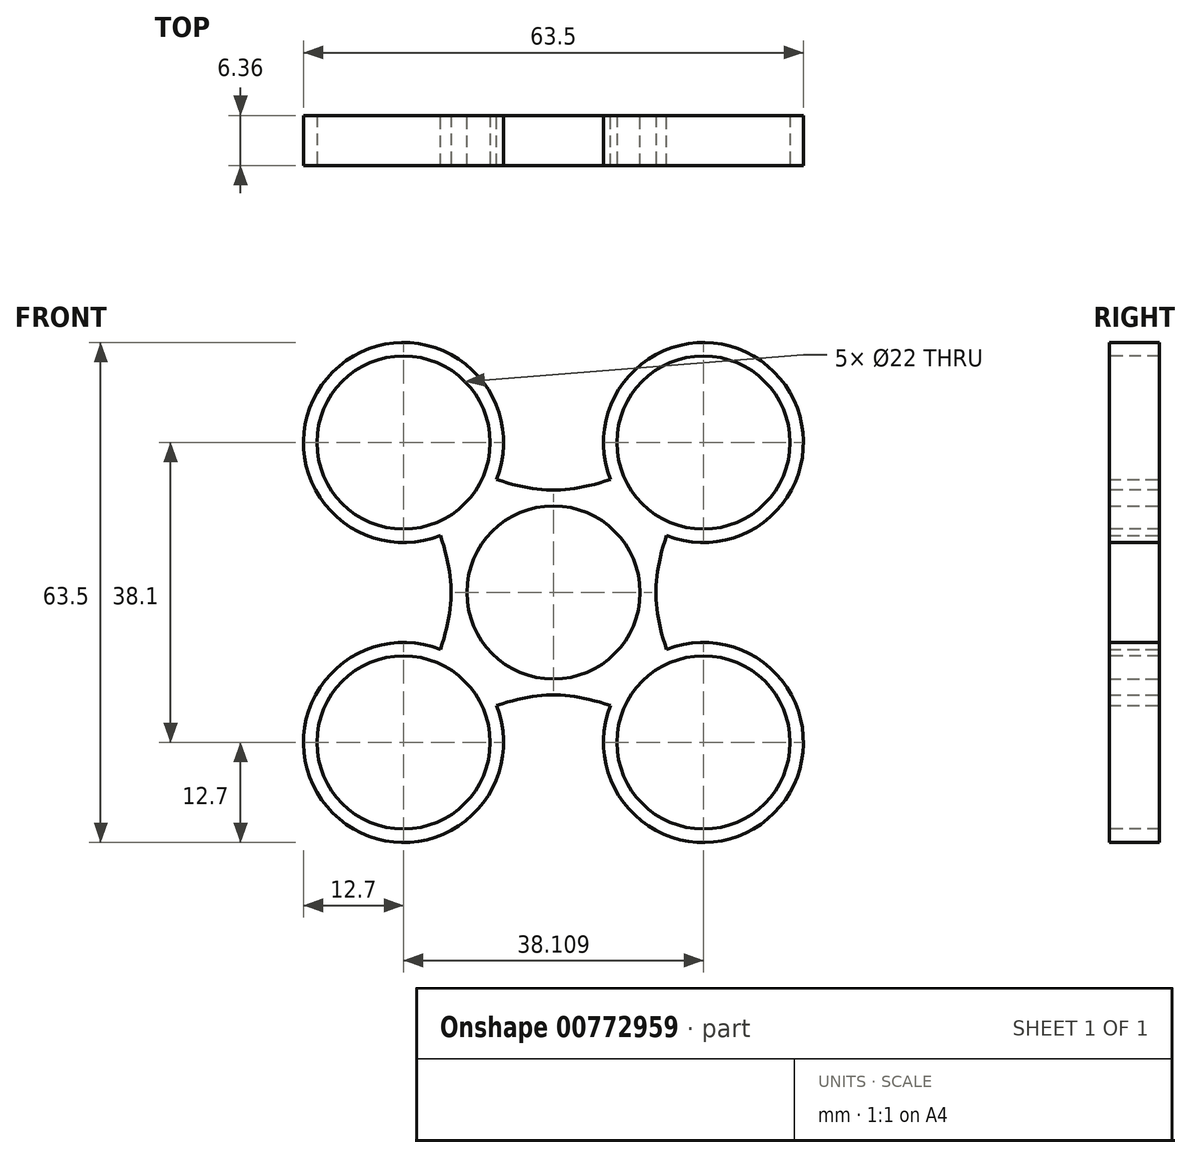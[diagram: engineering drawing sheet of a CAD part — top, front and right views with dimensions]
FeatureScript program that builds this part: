
annotation { "Feature Type Name" : "Feature", "Feature Type Description" : "" }
export const myFeature = defineFeature(function(context is Context, id is Id, definition is map)
    precondition{}
    {
        {
            var Q0;
            Q0=qCreatedBy(makeId("Front.planeOp"),FACE);
            var sketch = newSketch(context, id + "F0", { "sketchPlane" : qUnion([Q0])});
            skCircle(sketch, "E0", {"center": v(-19.05, 19.05) * mm, "radius": 12.7 * mm});
            skCircle(sketch, "E1", {"center": v(19.05, 19.05) * mm, "radius": 12.7 * mm});
            skCircle(sketch, "E2", {"center": v(19.05, -19.05) * mm, "radius": 12.7 * mm});
            skCircle(sketch, "E3", {"center": v(-19.05, -19.05) * mm, "radius": 12.7 * mm});
            skCircle(sketch, "E4", {"center": v(0, 0) * mm, "radius": 11 * mm});
            skFitSpline(sketch, "E5", {"points": [v(-19.05, -19.05) * mm, v(-19.05, 19.05) * mm], "startDerivative": vector(24.15, 57.15) * mm, "endDerivative": vector(-24.15, 57.15) * mm});
            skFitSpline(sketch, "E6", {"points": [v(-19.05, 19.05) * mm, v(19.05, 19.05) * mm], "startDerivative": vector(57.15, -24.15) * mm, "endDerivative": vector(57.15, 24.15) * mm});
            skFitSpline(sketch, "E7", {"points": [v(19.05, 19.05) * mm, v(19.05, -19.05) * mm], "startDerivative": vector(-24.15, -57.15) * mm, "endDerivative": vector(24.15, -57.15) * mm});
            skFitSpline(sketch, "E8", {"points": [v(-19.05, -19.05) * mm, v(19.05, -19.05) * mm], "startDerivative": vector(57.15, 24.15) * mm, "endDerivative": vector(57.15, -24.15) * mm});
            skSolve(sketch);
        }
        {
            var Q0;
            Q0=qCreatedBy(makeId("Front.planeOp"),FACE);
            var sketch = newSketch(context, id + "F1", { "sketchPlane" : qUnion([Q0])});
            skCircle(sketch, "E9", {"center": v(-19.05, 19.05) * mm, "radius": 11 * mm});
            skCircle(sketch, "E10", {"center": v(19.05, 19.05) * mm, "radius": 11 * mm});
            skCircle(sketch, "E11", {"center": v(-19.05, -19.05) * mm, "radius": 11 * mm});
            skCircle(sketch, "E12", {"center": v(19.06, -19.05) * mm, "radius": 11 * mm});
            skSolve(sketch);
        }
        {
            var Q0;
            Q0 = qSketchRegion(id + "F0", true);
            extrude(context, id + "F2", {"entities" : qUnion([Q0]), "endBound" : BoundingType.SYMMETRIC, "depth" : 6.35 * mm, "offsetDistance" : 25.4 * mm});
        }
        {
            var Q0;
            Q0 = qSketchRegion(id + "F1", true);
            extrude(context, id + "F3", {"entities" : qUnion([Q0]), "operationType" : NewBodyOperationType.REMOVE, "endBound" : BoundingType.SYMMETRIC, "oppositeDirection" : true, "depth" : 25.4 * mm, "offsetDistance" : 25.4 * mm});
        }
    });
